# Revit family: Sanitary_Showers_AXOR_12671XXX-AXOR-Starck-Nature-shower-column-with-overhead-shower-240-1jet-without-hand-shower
name_source: partatom
category: Plumbing Fixtures
revit_build: Autodesk Revit 2018 (Build: 20190510_1515(x64)
units: mm (PartAtom-declared; Revit-internal decimal feet)

## family parameters
Always vertical = No
Cut with Voids When Loaded = No
OmniClass Number = 23.31.17.00
OmniClass Title = Showers
Part Type = Normal
Room Calculation Point = No
Round Connector Dimension = Use Diameter
Shared = No
Work Plane-Based = Yes

## types (11) — shared parameters
Always visible = Yes
BIMobject category = Showers
Default Elevation = 1219.2 mm  [stored 4 ft]
Description = AXOR Starck Nature shower column with overhead shower 240 1jet without hand shower
Design country = Germany
Edition number = 1
IFC Classification = Sanitary Terminal
Manufacturer = AXOR
Manufacturer country = Germany
Manufacturer name = AXOR
Material main = Metal
Model = 12671XXX
OmniClass Code = 23-31 17 00
OmniClass Description = Showers
Product Guid = 28d42ea1-833b-4348-a1e2-b6f160aa7455
Product SKU = 12671XXX
Product data url = https://bimobject.com
Product family = AXOR Starck
Product group = Shower columns
Product name = 12671XXX AXOR Starck Nature shower column with overhead shower 240 1jet without hand shower
QR code = https://bimobject.com
URL = https://www.axor-design.com
Water Inlet = 12.7 mm  [stored 0.0416667 ft]
Water Inlet Description = Water Inlet 12.7mm

## per-type parameters (varying)
| type | Material |
| 809 Stainless Steel Optic | AXOR - Metal - 809 Stainless Steel Optic |
| 679 Matt Black | AXOR - Metal - 679 Matt Black |
| Polished Red Gold | AXOR - Metal - Polished Red Gold |
| Polished Gold Optic | AXOR - Metal - Polished Gold Optic |
| Polished Black Chrome | AXOR - Metal - Polished Black Chrome |
| Brushed Red Gold | AXOR - Metal - Brushed Red Gold |
| Brushed Nickel | AXOR - Metal - Brushed Nickel |
| Brushed Gold Optic | AXOR - Metal - Brushed Gold Optic |
| Brushed Bronze | AXOR - Metal - Brushed Bronze |
| Brushed Brass | AXOR - Metal - Brushed Brass |
| Brushed Black Chrome | AXOR - Metal - Brushed Black Chrome |

note: [stored X ft] marks values corroborated as IEEE doubles in the binary element streams (Revit-internal decimal feet)

## geometry (parser evidence)
native form markers: Sweep x3
no freeform markers — native parametric forms only
